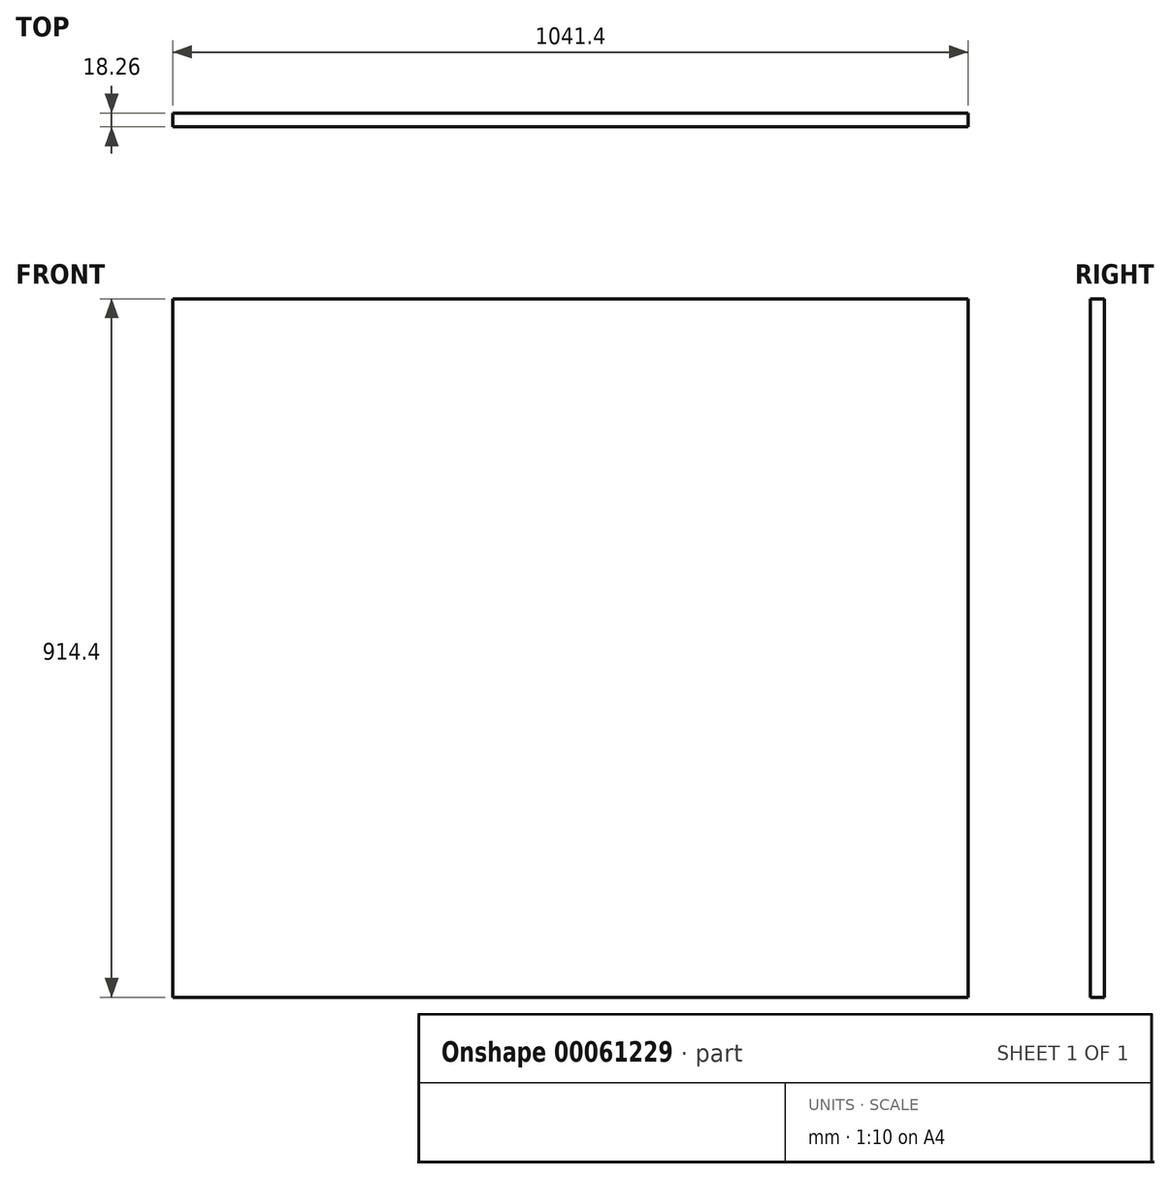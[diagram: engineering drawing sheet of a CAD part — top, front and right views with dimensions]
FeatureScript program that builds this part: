
annotation { "Feature Type Name" : "Feature", "Feature Type Description" : "" }
export const myFeature = defineFeature(function(context is Context, id is Id, definition is map)
    precondition{}
    {
        {
            var Q0;
            Q0=qCreatedBy(makeId("Front.planeOp"),FACE);
            var sketch = newSketch(context, id + "F0", { "sketchPlane" : qUnion([Q0])});
            skLineSegment(sketch, "E0.bottom", {"start": v(0, 0) * mm, "end": v(1041.4, 0) * mm});
            skLineSegment(sketch, "E0.top", {"start": v(0, 914.4) * mm, "end": v(1041.4, 914.4) * mm});
            skLineSegment(sketch, "E0.left", {"start": v(0, 0) * mm, "end": v(0, 914.4) * mm});
            skLineSegment(sketch, "E0.right", {"start": v(1041.4, 0) * mm, "end": v(1041.4, 914.4) * mm});
            skSolve(sketch);
        }
        {
            var Q0;
            Q0 = qSketchRegion(id + "F0", true);
            extrude(context, id + "F1", {"entities" : qUnion([Q0]), "depth" : 18.26 * mm});
        }
    });
